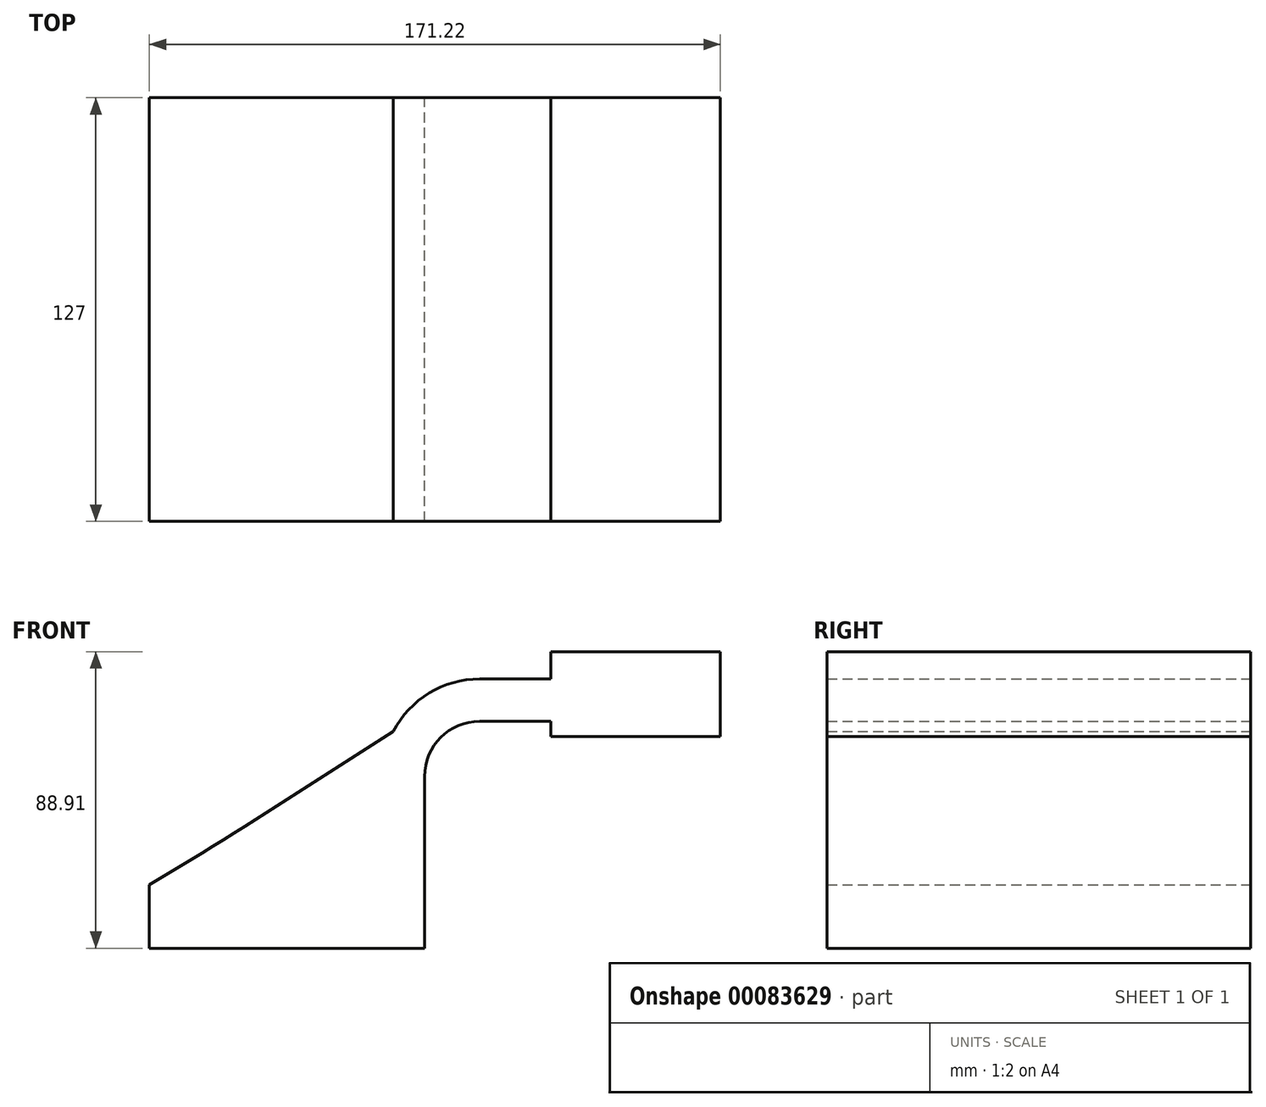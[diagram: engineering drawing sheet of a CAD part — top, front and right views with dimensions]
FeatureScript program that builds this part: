
annotation { "Feature Type Name" : "Feature", "Feature Type Description" : "" }
export const myFeature = defineFeature(function(context is Context, id is Id, definition is map)
    precondition{}
    {
        {
            var Q0;
            Q0=qCreatedBy(makeId("Front.planeOp"),FACE);
            var sketch = newSketch(context, id + "F0", { "sketchPlane" : qUnion([Q0])});
            skLineSegment(sketch, "E0.bottom", {"start": v(41.27, 9.53) * mm, "end": v(-41.28, 9.53) * mm});
            skLineSegment(sketch, "E0.top", {"start": v(41.28, -9.52) * mm, "end": v(-41.27, -9.52) * mm});
            skLineSegment(sketch, "E0.left", {"start": v(41.28, 9.53) * mm, "end": v(41.28, -9.52) * mm});
            skLineSegment(sketch, "E0.right", {"start": v(-41.28, 9.53) * mm, "end": v(-41.27, -9.52) * mm});
            skPoint(sketch, "E0.middle", {"position": v(0, 0) * mm});
            skLineSegment(sketch, "E1.bottom", {"start": v(79.14, 79.38) * mm, "end": v(129.94, 79.38) * mm});
            skLineSegment(sketch, "E1.top", {"start": v(79.14, 53.98) * mm, "end": v(129.94, 53.98) * mm});
            skLineSegment(sketch, "E1.left", {"start": v(79.14, 79.38) * mm, "end": v(79.14, 53.98) * mm});
            skLineSegment(sketch, "E1.right", {"start": v(129.94, 79.38) * mm, "end": v(129.94, 53.98) * mm});
            skPoint(sketch, "E1.middle", {"position": v(104.54, 66.67) * mm});
            skLineSegment(sketch, "E2", {"start": v(41.27, 9.53) * mm, "end": v(41.27, 41.99) * mm});
            skArc(sketch, "E3", {"start": v(41.27, 41.99) * mm, "mid": v(46.11, 53.66) * mm, "end": v(57.78, 58.5) * mm});
            skLineSegment(sketch, "E4", {"start": v(57.78, 58.5) * mm, "end": v(93.31, 58.5) * mm});
            skLineSegment(sketch, "E5.0", {"start": v(57.78, 71.2) * mm, "end": v(93.31, 71.2) * mm});
            skArc(sketch, "E5.1", {"start": v(28.57, 41.99) * mm, "mid": v(37.13, 62.64) * mm, "end": v(57.78, 71.2) * mm});
            skLineSegment(sketch, "E5.2", {"start": v(28.57, 9.53) * mm, "end": v(28.57, 41.99) * mm});
            skLineSegment(sketch, "E6", {"start": v(93.31, 71.2) * mm, "end": v(93.31, 58.5) * mm});
            skFitSpline(sketch, "E7", {"points": [v(-41.28, 9.52) * mm, v(57.78, 71.2) * mm], "startDerivative": vector(99.06, 57.64) * mm, "endDerivative": vector(99.06, 57.64) * mm});
            skSolve(sketch);
        }
        {
            var Q0;
            Q0 = qSketchRegion(id + "F0", true);
            extrude(context, id + "F1", {"entities" : qUnion([Q0]), "endBound" : BoundingType.SYMMETRIC, "depth" : 127 * mm, "hasSecondDirection" : true, "secondDirectionBound" : SecondDirectionBoundingType.UP_TO_SURFACE, "secondDirectionOppositeDirection" : true, "secondDirectionDepth" : 25.4 * mm});
        }
    });
